# Revit family: CONV_Zero_GnrlPrpseLmnrs_ThirtyWall_Ceiling
name_source: partatom
category: Lighting Fixtures
revit_build: Autodesk Revit 2015 (Build: 20140905_0730(x64)
units: mm (PartAtom-declared; Revit-internal decimal feet)

## types (4) — shared parameters
AssetType = Fixed
BIMObjectName = CONV_Zero_GnrlPrpseLmnrs_ThirtyWall_Ceiling
Brand = Zero
Category = Wall/ceiling
Collection = Thirty
Color Filter = 16777215
ConvergoRefNr = 0046-1708-0049-SE
Designer = Samuel Wilkinson
Dimming Lamp Color Temperature Shift = <None>
DurationUnit = Year
Emit Shape Visible in Rendering = No
Emit from Circle Diameter = 610 mm
ExpiringDate = 07/2018
Features = Terminal block 5x4 mm2
Finish = Painted aluminum
HasProtectiveEarth = No
IfcExportAs = IfcLightFixtureType
IfcExportType = NOTDEFINED
LensMaterial = Glass
LightFixtureMountingType = Surface
LightFixturePlacingType = Wall/ceiling
Manufacturer = Zero
ManufacturerName = Zero
ManufacturerURL = https://www.zerolighting.com
Material = Metal, glass
NBSDescription = General purpose luminaires
NBSReference = 90-60-50/405
Name = GnrlPrpseLmnrs_ThirtyWall_Ceiling
NominalCurrent = 0 A
NominalDiameter = 350 mm  [stored 1.14829 ft]
NominalFrequencyRange = 50 Hz
NominalHeight = 165 mm
NominalLength = 256 mm  [stored 0.839895 ft]
NominalRadius = 175 mm  [stored 0.574147 ft]
NominalVoltage = 230 V
NominalVoltageCalc = 0 V
NominalWidth = 231 mm  [stored 0.757874 ft]
NumberOfPoles = 1
PhaseAngle = 0.00°
Photometric Web File = Thirty82451.IES
Shape = Sculptured
Size = 164x215x247 mm
Tilt Angle = 90.00°
TotalWattage = 16 W
URL = https://www.zerolighting.com
Uniclass2 = Pr_70_70_49
Uniclass2015Description = Surface luminaires
Uniclass2015Reference = Pr_70_70_48_85
UsageCurrent = 0 A
Version = 1
VersionDate = 22/01/2018
WarrantyDurationUnit = Year
zero-valued in all types: Default Elevation, ElectricalDeviceNominalPower, MaintenanceFactor, NumberOfSources

## per-type parameters (varying)
| type | ArticleNumber | Color | Dimming | ModelNumber |
| Thirty LED 1043LM Black HFF | 8245-1-06HFF | Black | Dimmable with DALI, DSI, SwitchDim | 8245-1-06HFF |
| Thirty LED 1043LM Black | 8245-1-06 | Black | None | 8245-1-06 |
| Thirty LED 1043LM White | 8245-1-01 | White | None | 8245-1-01 |
| Thirty LED 1043LM White HFF | 8245-1-01HFF | White | Dimmable with DALI, DSI, SwitchDim | 8245-1-01HFF |

note: column(s) folded — value = type name in every type: Model

note: [stored X ft] marks values corroborated as IEEE doubles in the binary element streams (Revit-internal decimal feet)

## geometry (parser evidence)
native form markers: Sweep x5
no freeform markers — native parametric forms only
